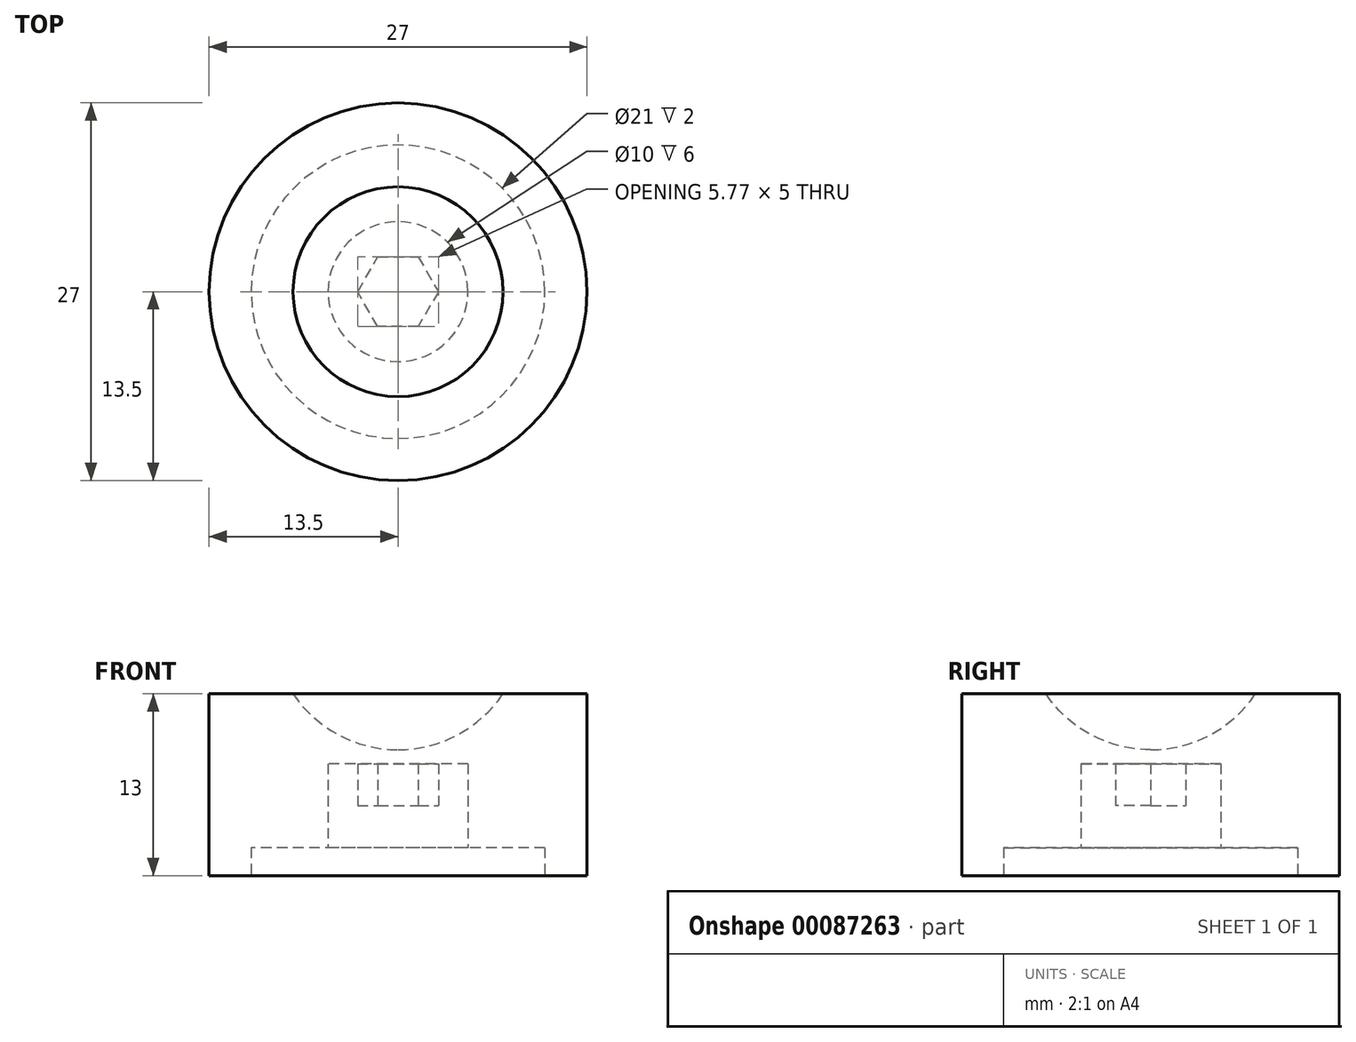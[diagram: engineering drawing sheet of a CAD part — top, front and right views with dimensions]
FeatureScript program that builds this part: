
annotation { "Feature Type Name" : "Feature", "Feature Type Description" : "" }
export const myFeature = defineFeature(function(context is Context, id is Id, definition is map)
    precondition{}
    {
        {
            var Q0;
            Q0=qCreatedBy(makeId("Top.planeOp"),FACE);
            var sketch = newSketch(context, id + "F0", { "sketchPlane" : qUnion([Q0])});
            skCircle(sketch, "E0", {"center": v(0, 0) * mm, "radius": 10.5 * mm});
            skCircle(sketch, "E1", {"center": v(0, 0) * mm, "radius": 5 * mm});
            skCircle(sketch, "E2.cCircle", {"center": v(0, 0) * mm, "radius": 2.5 * mm, "construction": true});
            skLineSegment(sketch, "E2.0", {"start": v(-1.44, 2.5) * mm, "end": v(1.44, 2.5) * mm});
            skLineSegment(sketch, "E2.1", {"start": v(1.44, 2.5) * mm, "end": v(2.89, 0) * mm});
            skLineSegment(sketch, "E2.2", {"start": v(2.89, 0) * mm, "end": v(1.44, -2.5) * mm});
            skLineSegment(sketch, "E2.3", {"start": v(1.44, -2.5) * mm, "end": v(-1.44, -2.5) * mm});
            skLineSegment(sketch, "E2.4", {"start": v(-1.44, -2.5) * mm, "end": v(-2.89, 0) * mm});
            skLineSegment(sketch, "E2.5", {"start": v(-2.89, 0) * mm, "end": v(-1.44, 2.5) * mm});
            skPoint(sketch, "E2.0.midPoint", {"position": v(0, 2.5) * mm});
            skSolve(sketch);
        }
        {
            var Q0;
            Q0=makeQuery(id+"F0.imprint","IMPRINT",FACE,{"disambiguationData":[TD([[makeQuery(id+"F0.imprint","IMPRINT",EDGE,{"derivedFrom":sQuery(id+"F0.wireOp",EDGE,"E1")}),1.0]])]});
            var Q1;
            Q1=makeQuery(id+"F0.imprint","IMPRINT",FACE,{"disambiguationData":[TD([[makeQuery(id+"F0.imprint","IMPRINT",EDGE,{"derivedFrom":sQuery(id+"F0.wireOp",EDGE,"E2.0")}),-1.0]])]});
            var Q2;
            Q2=makeQuery(id+"F0.imprint","IMPRINT",FACE,{"disambiguationData":[TD([[makeQuery(id+"F0.imprint","IMPRINT",EDGE,{"derivedFrom":sQuery(id+"F0.wireOp",EDGE,"E0")}),1.0]])]});
            extrude(context, id + "F1", {"entities" : qUnion([Q0, Q1, Q2]), "depth" : 2 * mm});
        }
        {
            var Q0;
            Q0=makeQuery(id+"F0.imprint","IMPRINT",FACE,{"disambiguationData":[TD([[makeQuery(id+"F0.imprint","IMPRINT",EDGE,{"derivedFrom":sQuery(id+"F0.wireOp",EDGE,"E1")}),1.0]])]});
            extrude(context, id + "F2", {"entities" : qUnion([Q0]), "operationType" : NewBodyOperationType.ADD, "depth" : 8 * mm});
        }
        {
            var Q0;
            Q0=makeQuery(id+"F0.imprint","IMPRINT",FACE,{"disambiguationData":[TD([[makeQuery(id+"F0.imprint","IMPRINT",EDGE,{"derivedFrom":sQuery(id+"F0.wireOp",EDGE,"E2.0")}),-1.0]])]});
            extrude(context, id + "F3", {"entities" : qUnion([Q0]), "operationType" : NewBodyOperationType.ADD, "depth" : 5 * mm});
        }
        {
            var Q0;
            Q0=qCreatedBy(makeId("Top.planeOp"),FACE);
            var sketch = newSketch(context, id + "F4", { "sketchPlane" : qUnion([Q0])});
            skCircle(sketch, "E3", {"center": v(0, 0) * mm, "radius": 13.5 * mm});
            skSolve(sketch);
        }
        {
            var Q0;
            Q0 = qSketchRegion(id + "F4", true);
            extrude(context, id + "F5", {"entities" : qUnion([Q0]), "depth" : 13 * mm});
        }
        {
            var Q0;
            Q0=makeQuery(id+"F1.opExtrude","SWEPT_BODY",BODY,{"disambiguationData":[OSD([sQuery(id+"F0.wireOp",EDGE,"E0")])]});
            var Q1;
            Q1=makeQuery(id+"F5.opExtrude","SWEPT_BODY",BODY,{"disambiguationData":[OSD([sQuery(id+"F4.wireOp",EDGE,"E3")])]});
            booleanBodies(context, id + "F6", {"operationType" : BooleanOperationType.SUBTRACTION, "tools" : qUnion([Q0]), "targets" : qUnion([Q1]), "keepTools" : true});
        }
        {
            var Q0;
            Q0=qCreatedBy(makeId("Right.planeOp"),FACE);
            var sketch = newSketch(context, id + "F7", { "sketchPlane" : qUnion([Q0])});
            skLineSegment(sketch, "E4", {"start": v(0, 13) * mm, "end": v(-7.5, 13) * mm});
            skArc(sketch, "E5", {"start": v(-7.5, 13) * mm, "mid": v(-4.25, 10.06) * mm, "end": v(0, 9) * mm});
            skLineSegment(sketch, "E6", {"start": v(0, 22.37) * mm, "end": v(0, 5.55) * mm, "construction": true});
            skPoint(sketch, "E7.orphan", {"position": v(7.5, 13) * mm});
            skLineSegment(sketch, "E8", {"start": v(0, 13) * mm, "end": v(0, 9) * mm});
            skSolve(sketch);
        }
        {
            var Q0;
            Q0=makeQuery(id+"F7.imprint","IMPRINT",FACE,{"disambiguationData":[TD([[makeQuery(id+"F7.imprint","IMPRINT",EDGE,{"derivedFrom":sQuery(id+"F7.wireOp",EDGE,"E4")}),1.0]])]});
            var Q1;
            Q1 = qConstructionFilter(qBodyType(qCreatedBy(id + "F7" ,EDGE), BodyType.WIRE), ConstructionObject.NO);
            var Q2;
            Q2=sQuery(id+"F7.wireOp",EDGE,"E6");
            revolve(context, id + "F8", {"operationType" : NewBodyOperationType.REMOVE, "entities" : qUnion([Q0]), "surfaceEntities" : qUnion([Q1]), "axis" : qUnion([Q2]), "revolveType" : RevolveType.FULL});
        }
    });
